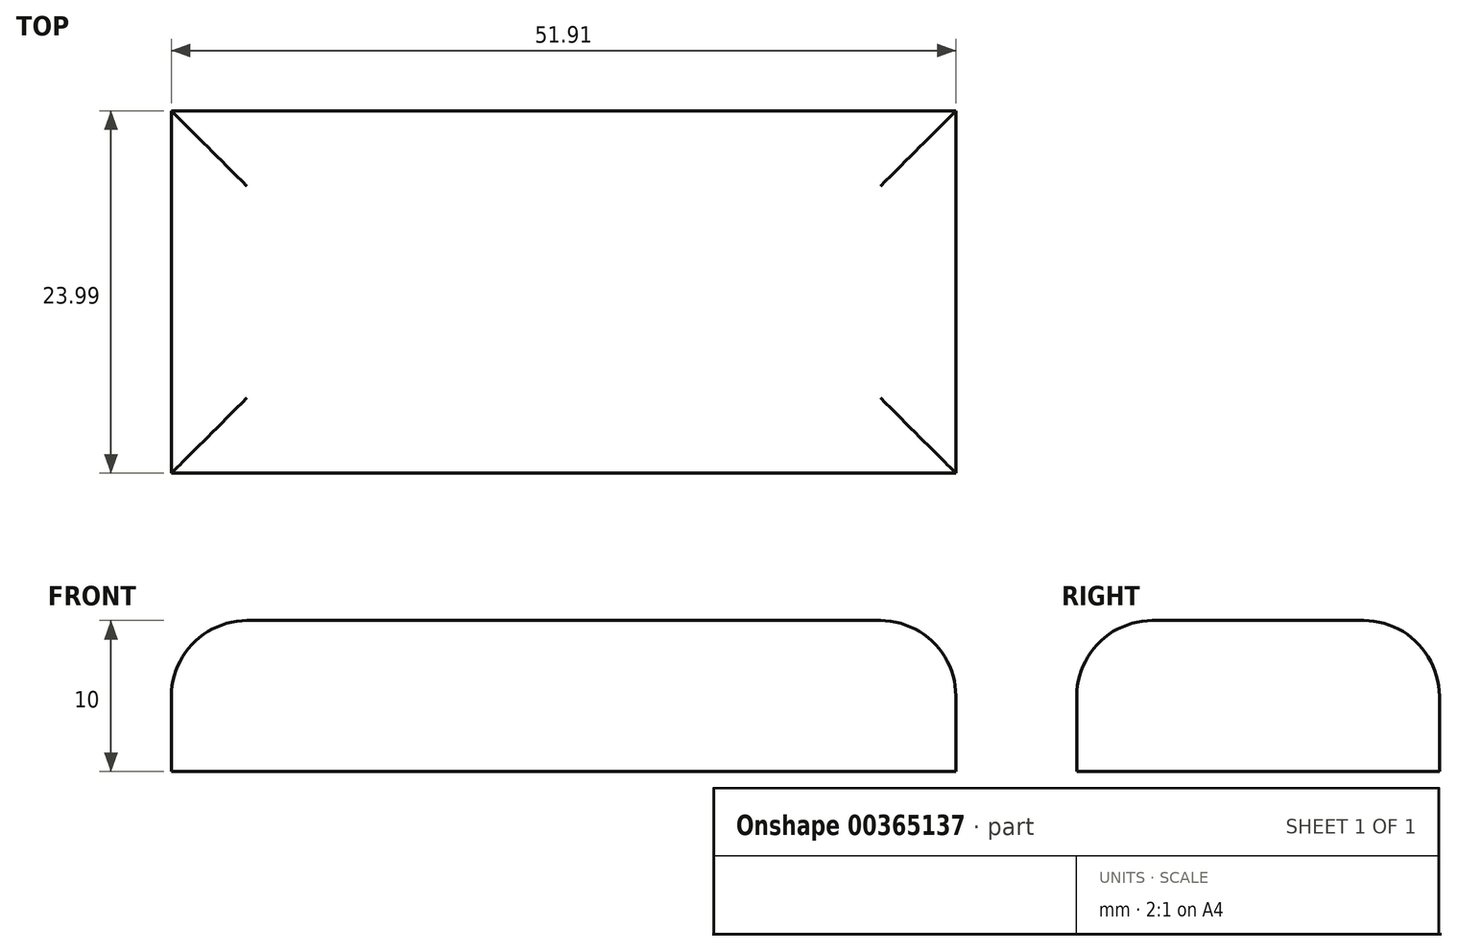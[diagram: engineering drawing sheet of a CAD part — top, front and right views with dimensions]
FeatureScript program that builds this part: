
annotation { "Feature Type Name" : "Feature", "Feature Type Description" : "" }
export const myFeature = defineFeature(function(context is Context, id is Id, definition is map)
    precondition{}
    {
        {
            var Q0;
            Q0=qCreatedBy(makeId("Top.planeOp"),FACE);
            var sketch = newSketch(context, id + "F0", { "sketchPlane" : qUnion([Q0])});
            skLineSegment(sketch, "E0.bottom", {"start": v(-10.58, -29.24) * mm, "end": v(41.33, -29.24) * mm});
            skLineSegment(sketch, "E0.top", {"start": v(-10.58, -53.23) * mm, "end": v(41.33, -53.23) * mm});
            skLineSegment(sketch, "E0.left", {"start": v(-10.58, -29.24) * mm, "end": v(-10.58, -53.23) * mm});
            skLineSegment(sketch, "E0.right", {"start": v(41.33, -29.24) * mm, "end": v(41.33, -53.23) * mm});
            skSolve(sketch);
        }
        {
            var Q0;
            Q0=makeQuery(id+"F0.imprint","IMPRINT",FACE,{"disambiguationData":[TD([[makeQuery(id+"F0.imprint","IMPRINT",EDGE,{"derivedFrom":sQuery(id+"F0.wireOp",EDGE,"E0.bottom")}),-1.0]])]});
            extrude(context, id + "F1", {"entities" : qUnion([Q0]), "depth" : 10 * mm});
        }
        {
            var Q0;
            Q0=makeQuery(id+"F1.opExtrude","CAP_EDGE",EDGE,{"disambiguationData":[OSD([sQuery(id+"F0.wireOp",EDGE,"E0.left")])],"isStart":false});
            var Q1;
            Q1=makeQuery(id+"F1.opExtrude","CAP_EDGE",EDGE,{"disambiguationData":[OSD([sQuery(id+"F0.wireOp",EDGE,"E0.right")])],"isStart":false});
            var Q2;
            Q2=makeQuery(id+"F1.opExtrude","CAP_EDGE",EDGE,{"disambiguationData":[OSD([sQuery(id+"F0.wireOp",EDGE,"E0.top")])],"isStart":false});
            var Q3;
            Q3=makeQuery(id+"F1.opExtrude","CAP_EDGE",EDGE,{"disambiguationData":[OSD([sQuery(id+"F0.wireOp",EDGE,"E0.bottom")])],"isStart":false});
            fillet(context, id + "F2", {"entities" : qUnion([Q0, Q1, Q2, Q3]), "radius" : 5 * mm, "tangentPropagation" : true, "allowEdgeOverflow" : false});
        }
    });
